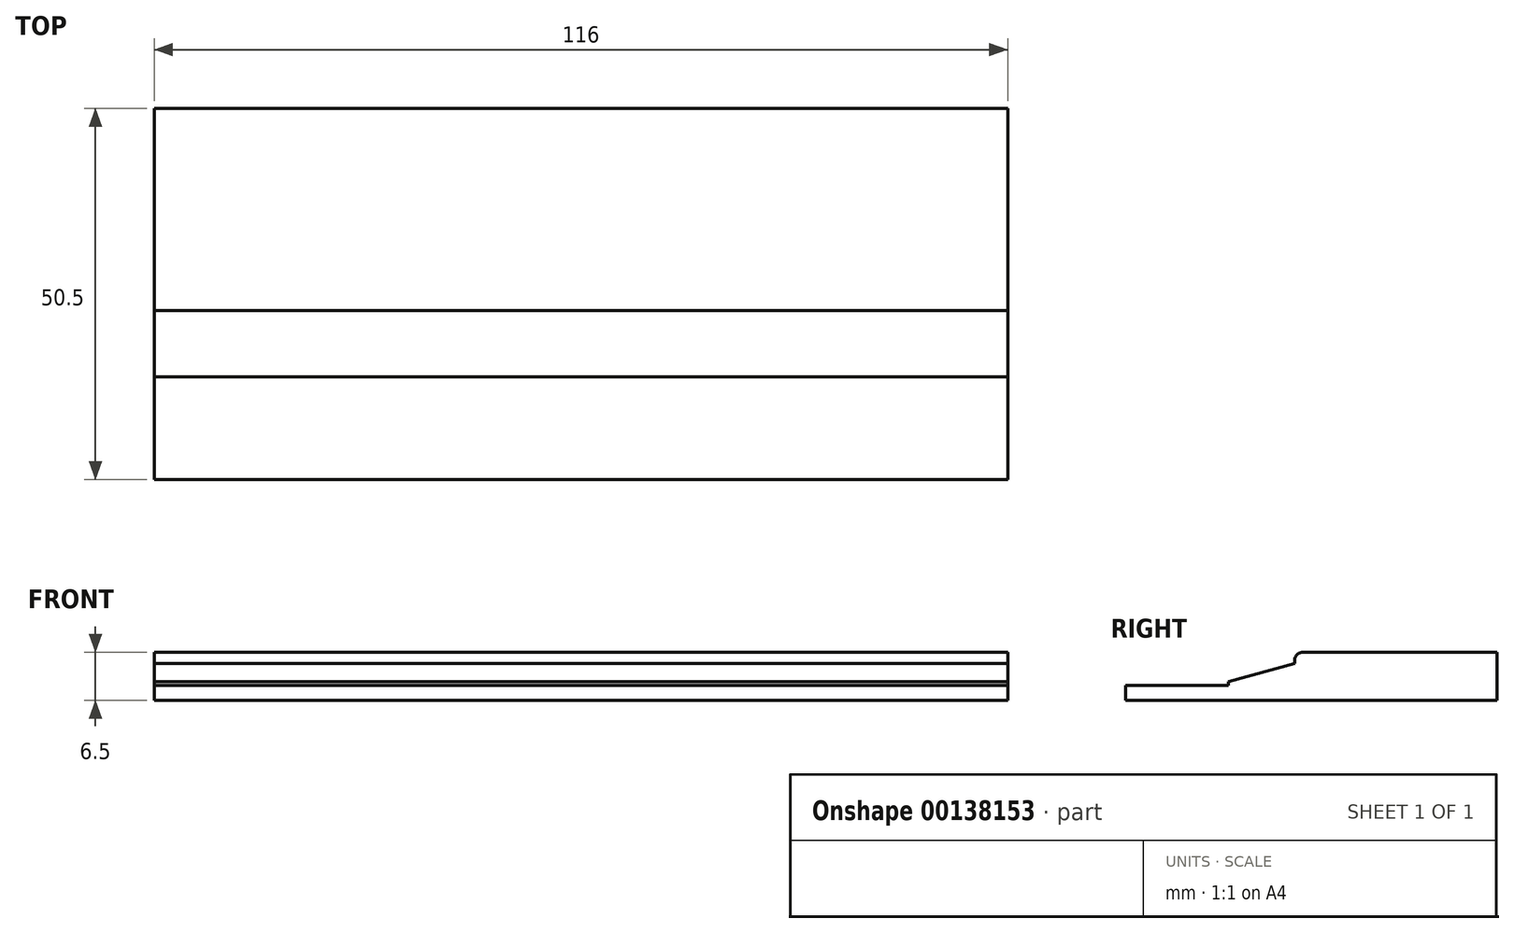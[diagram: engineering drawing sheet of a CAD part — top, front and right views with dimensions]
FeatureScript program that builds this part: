
annotation { "Feature Type Name" : "Feature", "Feature Type Description" : "" }
export const myFeature = defineFeature(function(context is Context, id is Id, definition is map)
    precondition{}
    {
        {
            var Q0;
            Q0=qCreatedBy(makeId("Right.planeOp"),FACE);
            var sketch = newSketch(context, id + "F0", { "sketchPlane" : qUnion([Q0])});
            skLineSegment(sketch, "E0", {"start": v(-49.24, 0) * mm, "end": v(1.26, 0) * mm});
            skLineSegment(sketch, "E1", {"start": v(1.26, 0) * mm, "end": v(1.26, 6.5) * mm});
            skLineSegment(sketch, "E2", {"start": v(-49.24, 0) * mm, "end": v(-49.24, 2) * mm});
            skLineSegment(sketch, "E3", {"start": v(-49.24, 2) * mm, "end": v(-35.24, 2) * mm});
            skLineSegment(sketch, "E4", {"start": v(-35.24, 2) * mm, "end": v(-35.24, 2.5) * mm});
            skPoint(sketch, "E5", {"position": v(-26.24, 0) * mm});
            skPoint(sketch, "E6", {"position": v(-26.24, 6.5) * mm});
            skLineSegment(sketch, "E7", {"start": v(1.26, 6.5) * mm, "end": v(-26.24, 6.5) * mm});
            skLineSegment(sketch, "E8", {"start": v(-26.24, 5) * mm, "end": v(-26.24, 6.5) * mm});
            skLineSegment(sketch, "E9", {"start": v(-35.24, 2.5) * mm, "end": v(-26.24, 5) * mm});
            skSolve(sketch);
        }
        {
            var Q0;
            Q0=makeQuery(id+"F0.imprint","IMPRINT",FACE,{"disambiguationData":[TD([[makeQuery(id+"F0.imprint","IMPRINT",EDGE,{"derivedFrom":sQuery(id+"F0.wireOp",EDGE,"E0")}),1.0]])]});
            extrude(context, id + "F1", {"entities" : qUnion([Q0]), "depth" : 116 * mm});
        }
        {
            var Q0;
            Q0=makeQuery(id+"F1.opExtrude","SWEPT_EDGE",EDGE,{"disambiguationData":[OSD([sQuery(id+"F0.wireOp",EDGE,"E7"),sQuery(id+"F0.wireOp",EDGE,"E8")])]});
            fillet(context, id + "F2", {"entities" : qUnion([Q0]), "radius" : 1 * mm, "tangentPropagation" : true, "allowEdgeOverflow" : false});
        }
    });
